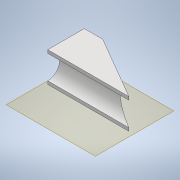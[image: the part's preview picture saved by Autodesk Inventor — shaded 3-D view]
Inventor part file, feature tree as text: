
AUTODESK INVENTOR PART (.ipt)
format: ipt  version: 2022.3 (Build 263350000, 350)  size: 128,512 bytes
history: native  units: mm
features: thicken_offset x4, extrude x3, sketch x3, other x2, plane x1, reference x1
ambient origin geometry x8: Origin, YZ Plane, XZ Plane, XY Plane, X Axis, Y Axis, Z Axis, Center Point
bodies: Solid1 (feature_tree)
feature tree (14):
  plane  "Work Plane1"
  extrude  "Extrusion1"  Depth=6.0mm
  extrude  "Extrusion2"  Depth=0.2mm
  thicken_offset  "Thicken1"
  thicken_offset  "Thicken2"
  extrude  "Extrusion3"  Depth=0.2mm
  thicken_offset  "Thicken3"
  thicken_offset  "Thicken4"
  sketch  "Sketch1"  dims[d0=8.0mm d1=0.0mm d2=6.0mm]
  reference  "Reference1"
  sketch  "Sketch2"  dims[d3=15.981mm d4=0.0mm d5=0.2mm]
  sketch  "Sketch3"  dims[d6=0.2mm d7=0.2mm d8=0.2mm d9=0.0mm d10=0.0mm d11=0.2mm d12=0.2mm d13=0.2mm d14=0.2mm]
  other  "v2.0.iam"
  other  "Base:1"
